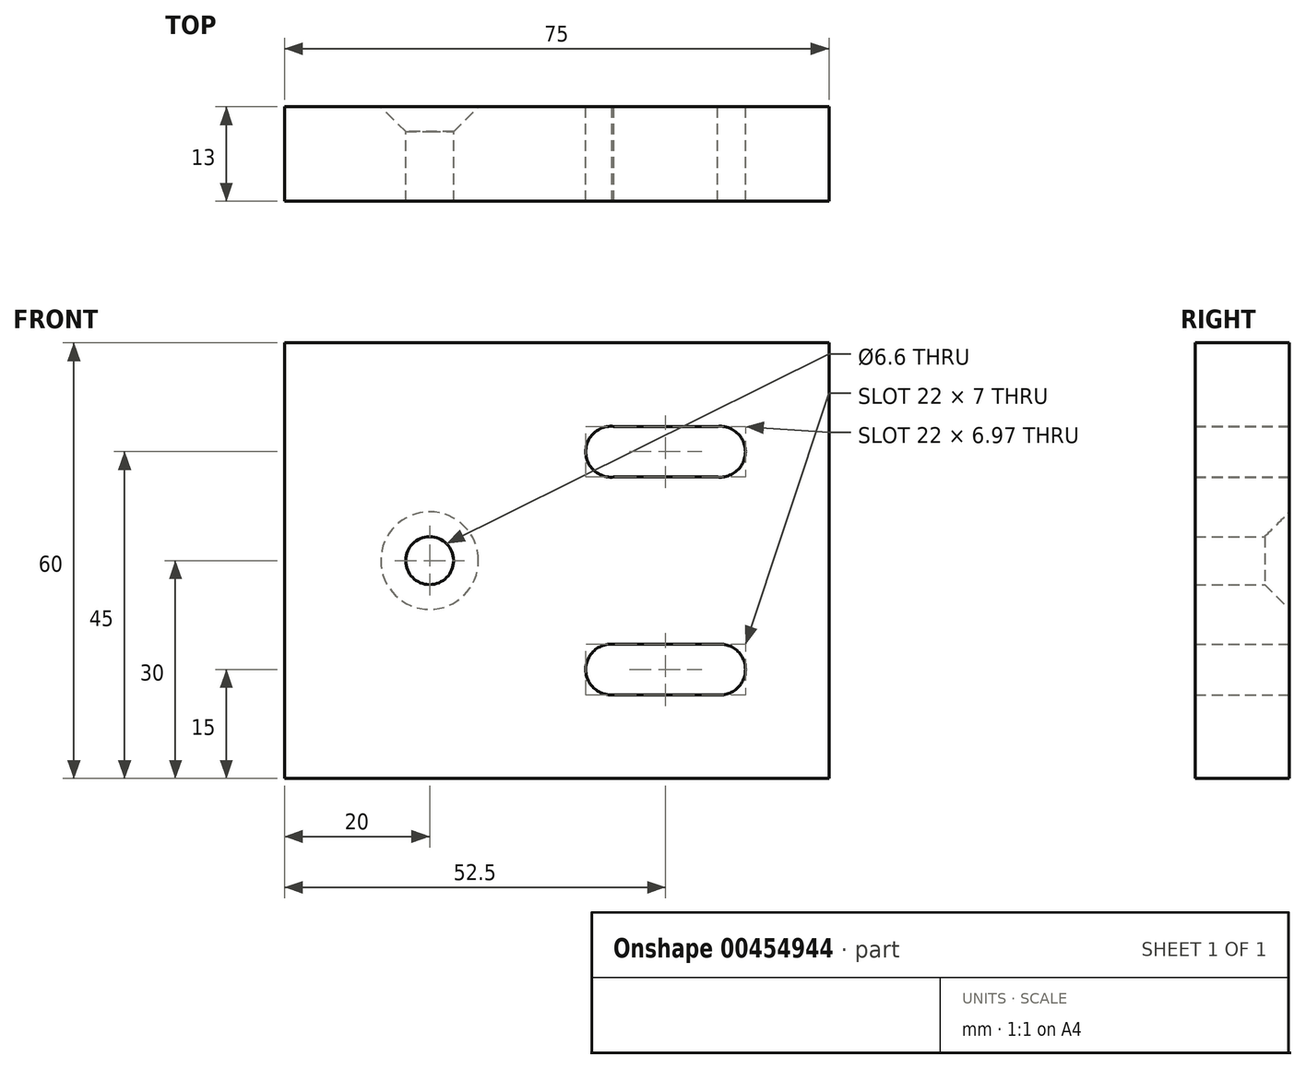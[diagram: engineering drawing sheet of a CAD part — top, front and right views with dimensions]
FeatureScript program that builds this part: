
annotation { "Feature Type Name" : "Feature", "Feature Type Description" : "" }
export const myFeature = defineFeature(function(context is Context, id is Id, definition is map)
    precondition{}
    {
        {
            var Q0;
            Q0=qCreatedBy(makeId("Front.planeOp"),FACE);
            var sketch = newSketch(context, id + "F0", { "sketchPlane" : qUnion([Q0])});
            skLineSegment(sketch, "E0.bottom", {"start": v(0, 0) * mm, "end": v(75, 0) * mm});
            skLineSegment(sketch, "E0.top", {"start": v(0, -60) * mm, "end": v(75, -60) * mm});
            skLineSegment(sketch, "E0.left", {"start": v(0, 0) * mm, "end": v(0, -60) * mm});
            skLineSegment(sketch, "E0.right", {"start": v(75, 0) * mm, "end": v(75, -60) * mm});
            skSolve(sketch);
        }
        {
            var Q0;
            Q0 = qSketchRegion(id + "F0", true);
            var Q1;
            Q1=makeQuery(id+"F0.imprint","IMPRINT",FACE,{"disambiguationData":[TD([[makeQuery(id+"F0.imprint","IMPRINT",EDGE,{"derivedFrom":sQuery(id+"F0.wireOp",EDGE,"E0.bottom")}),-1.0]])]});
            extrude(context, id + "F1", {"entities" : qUnion([Q0, Q1]), "depth" : 13 * mm});
        }
        {
            var Q0;
            Q0=makeQuery(id+"F1.opExtrude","CAP_FACE",FACE,{"disambiguationData":[OSD([sQuery(id+"F0.wireOp",EDGE,"E0.bottom"),sQuery(id+"F0.wireOp",EDGE,"E0.top"),sQuery(id+"F0.wireOp",EDGE,"E0.left"),sQuery(id+"F0.wireOp",EDGE,"E0.right")])],"isStart":true});
            var sketch = newSketch(context, id + "F2", { "sketchPlane" : qUnion([Q0])});
            skPoint(sketch, "E1", {"position": v(-20, -30) * mm});
            skSolve(sketch);
        }
        {
            var Q0;
            Q0=sQuery(id+"F2.wireOp",VERTEX,"E1");
            var Q1;
            Q1=makeQuery(id+"F1.opExtrude","SWEPT_BODY",BODY,{"disambiguationData":[OSD([sQuery(id+"F0.wireOp",EDGE,"E0.bottom"),sQuery(id+"F0.wireOp",EDGE,"E0.top"),sQuery(id+"F0.wireOp",EDGE,"E0.left"),sQuery(id+"F0.wireOp",EDGE,"E0.right")])]});
            hole(context, id + "F3", {"style" : HoleStyle.C_SINK, "endStyle" : HoleEndStyle.THROUGH, "standardTappedOrClearance" : lookupTablePath({ "standard" : "ISO", "fit" : "Normal", "size" : "M6", "type" : "Clearance" }), "standardBlindInLast" : lookupTablePath({ "fit" : "Standard", "standard" : "ISO", "size" : "M6", "type" : "Clearance" }), "holeDiameter" : 6.6 * mm, "cSinkDiameter" : 13.44 * mm, "cSinkAngle" : 90 * degree, "isTappedThrough" : true, "tappedDepth" : 50 * mm, "tapClearance" : 3, "startFromSketch" : true, "locations" : qUnion([Q0]), "scope" : qUnion([Q1])});
        }
        {
            var Q0;
            Q0=makeQuery(id+"F1.opExtrude","CAP_FACE",FACE,{"disambiguationData":[OSD([sQuery(id+"F0.wireOp",EDGE,"E0.bottom"),sQuery(id+"F0.wireOp",EDGE,"E0.top"),sQuery(id+"F0.wireOp",EDGE,"E0.left"),sQuery(id+"F0.wireOp",EDGE,"E0.right")])],"isStart":true});
            var sketch = newSketch(context, id + "F4", { "sketchPlane" : qUnion([Q0])});
            skPoint(sketch, "E2", {"position": v(-60, -45) * mm});
            skPoint(sketch, "E3", {"position": v(-45, -45) * mm});
            skPoint(sketch, "E4", {"position": v(-60, -15) * mm});
            skPoint(sketch, "E5", {"position": v(-45, -15) * mm});
            skSolve(sketch);
        }
        {
            var Q0;
            Q0=sQuery(id+"F4.wireOp",VERTEX,"E3");
            var Q1;
            Q1=sQuery(id+"F4.wireOp",VERTEX,"E2");
            var Q2;
            Q2=sQuery(id+"F4.wireOp",VERTEX,"E4");
            var Q3;
            Q3=sQuery(id+"F4.wireOp",VERTEX,"E5");
            var Q4;
            Q4=makeQuery(id+"F1.opExtrude","SWEPT_BODY",BODY,{"disambiguationData":[OSD([sQuery(id+"F0.wireOp",EDGE,"E0.bottom"),sQuery(id+"F0.wireOp",EDGE,"E0.top"),sQuery(id+"F0.wireOp",EDGE,"E0.left"),sQuery(id+"F0.wireOp",EDGE,"E0.right")])]});
            hole(context, id + "F5", {"style" : HoleStyle.SIMPLE, "endStyle" : HoleEndStyle.THROUGH, "holeDiameter" : 7 * mm, "isTappedThrough" : true, "tappedDepth" : 50 * mm, "tapClearance" : 3, "startFromSketch" : true, "locations" : qUnion([Q0, Q1, Q2, Q3]), "scope" : qUnion([Q4])});
        }
        {
            var Q0;
            Q0=makeQuery(id+"F1.opExtrude","CAP_FACE",FACE,{"disambiguationData":[OSD([sQuery(id+"F0.wireOp",EDGE,"E0.bottom"),sQuery(id+"F0.wireOp",EDGE,"E0.top"),sQuery(id+"F0.wireOp",EDGE,"E0.left"),sQuery(id+"F0.wireOp",EDGE,"E0.right")])],"isStart":true});
            var sketch = newSketch(context, id + "F6", { "sketchPlane" : qUnion([Q0])});
            skLineSegment(sketch, "E6", {"start": v(-45.1, -48.5) * mm, "end": v(-60, -48.5) * mm});
            skLineSegment(sketch, "E7", {"start": v(-60, -48.5) * mm, "end": v(-60, -41.5) * mm});
            skLineSegment(sketch, "E8", {"start": v(-60, -41.5) * mm, "end": v(-45, -41.5) * mm});
            skLineSegment(sketch, "E9", {"start": v(-45, -41.5) * mm, "end": v(-45.1, -48.5) * mm});
            skSolve(sketch);
        }
        {
            var Q0;
            Q0 = qSketchRegion(id + "F6", true);
            extrude(context, id + "F7", {"entities" : qUnion([Q0]), "operationType" : NewBodyOperationType.REMOVE, "oppositeDirection" : true, "depth" : 25 * mm});
        }
        {
            var Q0;
            Q0=makeQuery(id+"F1.opExtrude","CAP_FACE",FACE,{"disambiguationData":[OSD([sQuery(id+"F0.wireOp",EDGE,"E0.bottom"),sQuery(id+"F0.wireOp",EDGE,"E0.top"),sQuery(id+"F0.wireOp",EDGE,"E0.left"),sQuery(id+"F0.wireOp",EDGE,"E0.right")])],"isStart":true});
            var sketch = newSketch(context, id + "F8", { "sketchPlane" : qUnion([Q0])});
            skLineSegment(sketch, "E10", {"start": v(-59.66, -11.52) * mm, "end": v(-45.34, -11.52) * mm});
            skLineSegment(sketch, "E11", {"start": v(-45.34, -11.52) * mm, "end": v(-45.34, -18.48) * mm});
            skLineSegment(sketch, "E12", {"start": v(-45.34, -18.48) * mm, "end": v(-59.66, -18.48) * mm});
            skLineSegment(sketch, "E13", {"start": v(-59.66, -18.48) * mm, "end": v(-59.66, -11.52) * mm});
            skSolve(sketch);
        }
        {
            var Q0;
            {var subQ0=sQuery(id+"F8.wireOp",EDGE,"E10");Q0=makeQuery(id+"F8.imprint","IMPRINT",FACE,{"disambiguationData":[TD([[makeQuery(id+"F8.imprint","IMPRINT",EDGE,{"derivedFrom":subQ0}),-1.0]])]});}
            extrude(context, id + "F9", {"entities" : qUnion([Q0]), "operationType" : NewBodyOperationType.REMOVE, "oppositeDirection" : true, "depth" : 25 * mm});
        }
    });
